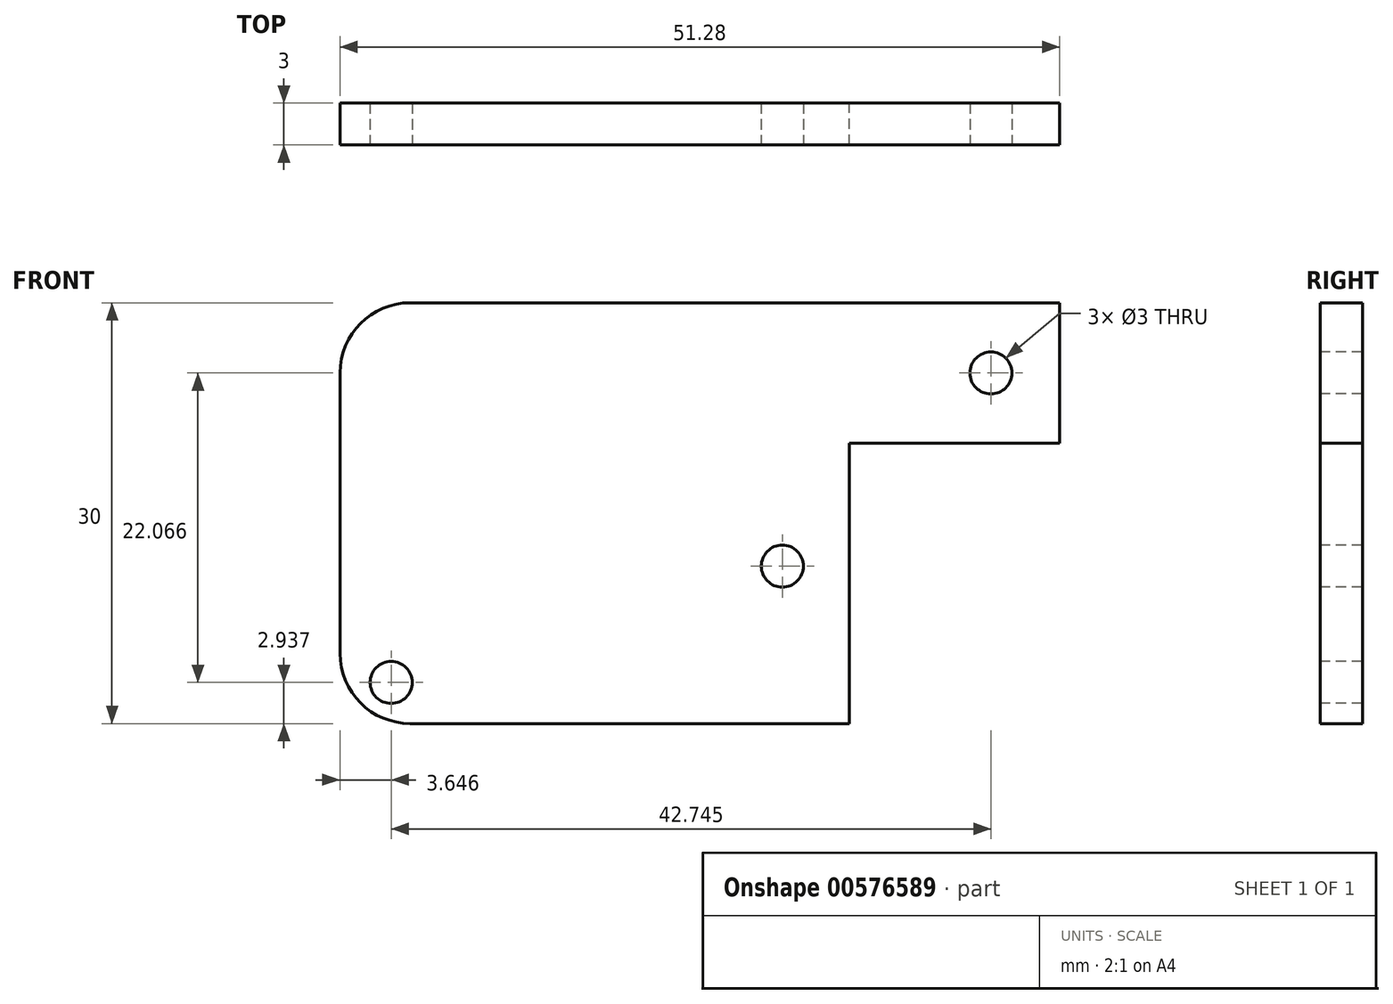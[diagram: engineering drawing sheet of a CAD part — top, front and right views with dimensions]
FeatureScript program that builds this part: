
annotation { "Feature Type Name" : "Feature", "Feature Type Description" : "" }
export const myFeature = defineFeature(function(context is Context, id is Id, definition is map)
    precondition{}
    {
        {
            var Q0;
            Q0=qCreatedBy(makeId("Front.planeOp"),FACE);
            var sketch = newSketch(context, id + "F0", { "sketchPlane" : qUnion([Q0])});
            skLineSegment(sketch, "E0", {"start": v(-45.64, -20.26) * mm, "end": v(-45.64, 9.74) * mm});
            skLineSegment(sketch, "E1", {"start": v(-45.64, 9.74) * mm, "end": v(5.64, 9.74) * mm});
            skLineSegment(sketch, "E2", {"start": v(5.64, 9.74) * mm, "end": v(5.64, -0.26) * mm});
            skLineSegment(sketch, "E3", {"start": v(5.64, -0.26) * mm, "end": v(-9.36, -0.26) * mm});
            skLineSegment(sketch, "E4", {"start": v(-9.36, -0.26) * mm, "end": v(-9.36, -20.26) * mm});
            skLineSegment(sketch, "E5", {"start": v(-9.36, -20.26) * mm, "end": v(-45.64, -20.26) * mm});
            skSolve(sketch);
        }
        {
            var Q0;
            Q0 = qSketchRegion(id + "F0", true);
            extrude(context, id + "F1", {"entities" : qUnion([Q0]), "depth" : 3 * mm, "offsetDistance" : 25 * mm});
        }
        {
            var Q0;
            Q0=makeQuery(id+"F1.opExtrude","CAP_FACE",FACE,{"disambiguationData":[OSD([sQuery(id+"F0.wireOp",EDGE,"E0"),sQuery(id+"F0.wireOp",EDGE,"E1"),sQuery(id+"F0.wireOp",EDGE,"E2"),sQuery(id+"F0.wireOp",EDGE,"E3"),sQuery(id+"F0.wireOp",EDGE,"E4"),sQuery(id+"F0.wireOp",EDGE,"E5")])],"isStart":false});
            var sketch = newSketch(context, id + "F2", { "sketchPlane" : qUnion([Q0])});
            skPoint(sketch, "E6", {"position": v(-42, -17.32) * mm});
            skPoint(sketch, "E7", {"position": v(-14.12, -9.03) * mm});
            skPoint(sketch, "E8", {"position": v(0.75, 4.74) * mm});
            skPoint(sketch, "E8.positionSnap0", {"position": v(5.64, 4.74) * mm});
            skSolve(sketch);
        }
        {
            var Q0;
            Q0=sQuery(id+"F2.wireOp",VERTEX,"E6");
            var Q1;
            Q1=sQuery(id+"F2.wireOp",VERTEX,"E7");
            var Q2;
            Q2=sQuery(id+"F2.wireOp",VERTEX,"E8");
            var Q3;
            Q3=makeQuery(id+"F1.opExtrude","SWEPT_BODY",BODY,{"disambiguationData":[OSD([sQuery(id+"F0.wireOp",EDGE,"E0"),sQuery(id+"F0.wireOp",EDGE,"E1"),sQuery(id+"F0.wireOp",EDGE,"E2"),sQuery(id+"F0.wireOp",EDGE,"E3"),sQuery(id+"F0.wireOp",EDGE,"E4"),sQuery(id+"F0.wireOp",EDGE,"E5")])]});
            hole(context, id + "F3", {"style" : HoleStyle.SIMPLE, "endStyle" : HoleEndStyle.THROUGH, "holeDiameter" : 3 * mm, "isTappedThrough" : true, "tappedDepth" : 12 * mm, "tapClearance" : 3, "locations" : qUnion([Q0, Q1, Q2]), "scope" : qUnion([Q3])});
        }
        {
            var Q0;
            Q0=makeQuery(id+"F1.opExtrude","SWEPT_EDGE",EDGE,{"disambiguationData":[OSD([sQuery(id+"F0.wireOp",EDGE,"E0"),sQuery(id+"F0.wireOp",EDGE,"E1")])]});
            var Q1;
            Q1=makeQuery(id+"F1.opExtrude","SWEPT_EDGE",EDGE,{"disambiguationData":[OSD([sQuery(id+"F0.wireOp",EDGE,"E0"),sQuery(id+"F0.wireOp",EDGE,"E5")])]});
            fillet(context, id + "F4", {"entities" : qUnion([Q0, Q1]), "radius" : 5 * mm, "tangentPropagation" : true, "allowEdgeOverflow" : false});
        }
    });
